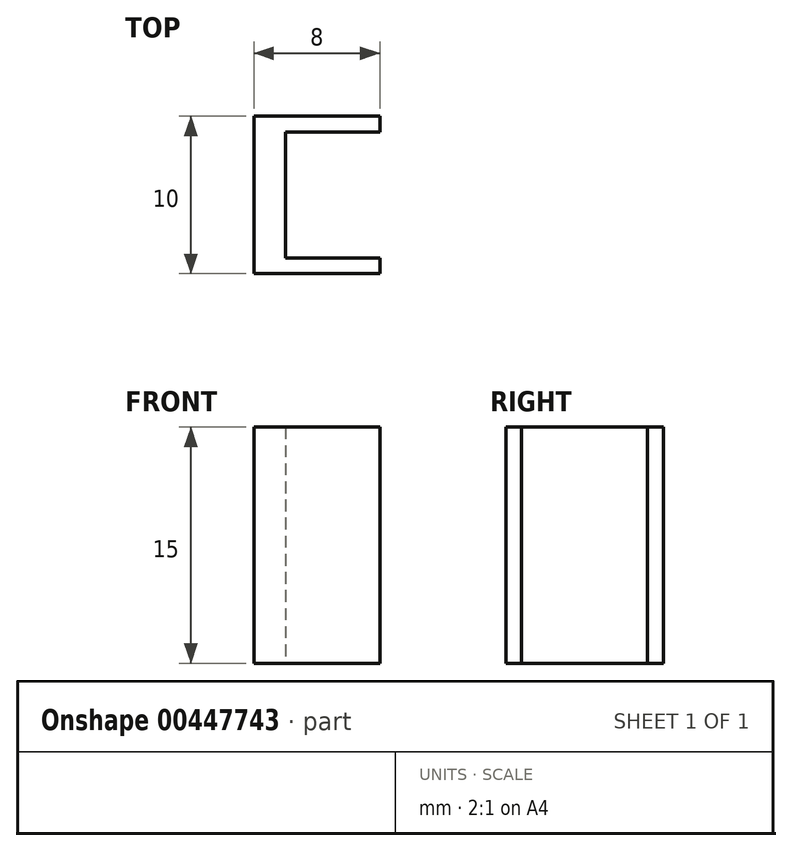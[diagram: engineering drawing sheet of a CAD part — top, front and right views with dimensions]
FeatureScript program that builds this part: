
annotation { "Feature Type Name" : "Feature", "Feature Type Description" : "" }
export const myFeature = defineFeature(function(context is Context, id is Id, definition is map)
    precondition{}
    {
        {
            var Q0;
            Q0=qCreatedBy(makeId("Top.planeOp"),FACE);
            var sketch = newSketch(context, id + "F0", { "sketchPlane" : qUnion([Q0])});
            skLineSegment(sketch, "E0", {"start": v(0, 0) * mm, "end": v(0, 10) * mm});
            skLineSegment(sketch, "E1", {"start": v(0, 10) * mm, "end": v(8, 10) * mm});
            skLineSegment(sketch, "E2", {"start": v(8, 10) * mm, "end": v(8, 9) * mm});
            skLineSegment(sketch, "E3", {"start": v(8, 9) * mm, "end": v(2, 9) * mm});
            skLineSegment(sketch, "E4", {"start": v(0, 0) * mm, "end": v(8, 0) * mm});
            skLineSegment(sketch, "E5", {"start": v(8, 0) * mm, "end": v(8, 1) * mm});
            skLineSegment(sketch, "E6", {"start": v(8, 1) * mm, "end": v(2, 1) * mm});
            skLineSegment(sketch, "E7", {"start": v(2, 1) * mm, "end": v(2, 9) * mm});
            skSolve(sketch);
        }
        {
            var Q0;
            Q0=makeQuery(id+"F0.imprint","IMPRINT",FACE,{"disambiguationData":[TD([[makeQuery(id+"F0.imprint","IMPRINT",EDGE,{"derivedFrom":sQuery(id+"F0.wireOp",EDGE,"E0")}),-1.0]])]});
            extrude(context, id + "F1", {"entities" : qUnion([Q0]), "depth" : 15 * mm});
        }
    });
